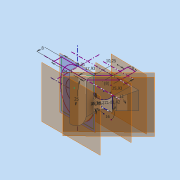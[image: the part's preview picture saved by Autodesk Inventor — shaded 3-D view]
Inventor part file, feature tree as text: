
AUTODESK INVENTOR PART (.ipt)
format: ipt  version: 2019 (Build 230136000, 136)  size: 334,848 bytes
history: native  units: mm
features: other x10, sketch x6, extrude x5, loft x2, chamfer x1, shell x1, projected_geometry x1
ambient origin geometry x8: Origin, YZ Plane, XZ Plane, XY Plane, X Axis, Y Axis, Z Axis, Center Point
bodies: Body1 (feature_tree), Body2 (feature_tree), Body3 (feature_tree)
feature tree (26):
  other  "Твердое тело1"
  other  "Основной эскиз"
  extrude  "Выдавливание1"  Depth=34.31mm
  sketch  "Эскиз7"
  extrude  "Эллипс"  Depth=8.0mm
  other  "РабПлоскость18"
  sketch  "Эскиз19"
  extrude  "Дырки"  Depth=34.31mm
  chamfer  "Фаска для дырок"  Distance=8.0mm
  shell  "Оболочка12"  Thickness=17.93mm
  other  "РабПлоскость33"
  other  "РабПлоскость34"
  sketch  "Эскиз26"
  extrude  "Выдавливание23"  Depth=25.93mm
  other  "РабПлоскость40"
  loft  "Лофт15"
  loft  "Лофт16"
  sketch  "Эскиз35"
  extrude  "Выдавливание29"  Depth=49.49mm TaperAngle=0.0deg
  other  "РабПлоскость39"
  sketch  "Эскиз33"
  projected_geometry  "Спроецированная петля6"
  sketch  "Эскиз34"
  other  "Ребра33"
  other  "Ребра34"
  other  "Твердое тело17"
